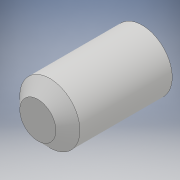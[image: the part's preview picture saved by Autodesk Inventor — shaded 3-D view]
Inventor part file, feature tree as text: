
AUTODESK INVENTOR PART (.ipt)
format: ipt  version: 2018 (Build 220112000, 112)  size: 128,512 bytes
history: native  units: mm
features: sketch x3, extrude x2, chamfer x1
ambient origin geometry x8: Origin, YZ Plane, XZ Plane, XY Plane, X Axis, Y Axis, Z Axis, Center Point
bodies: Solide1 (feature_tree)
feature tree (6):
  extrude  "Extrusion1"  Depth=15.0mm
  chamfer  "Chanfrein1"  Distance=26.0mm
  extrude  "Extrusion2"  Depth=2.0mm TaperAngle=45.0deg
  sketch  "Esquisse3"
  sketch  "Esquisse1"
  sketch  "Esquisse2"
